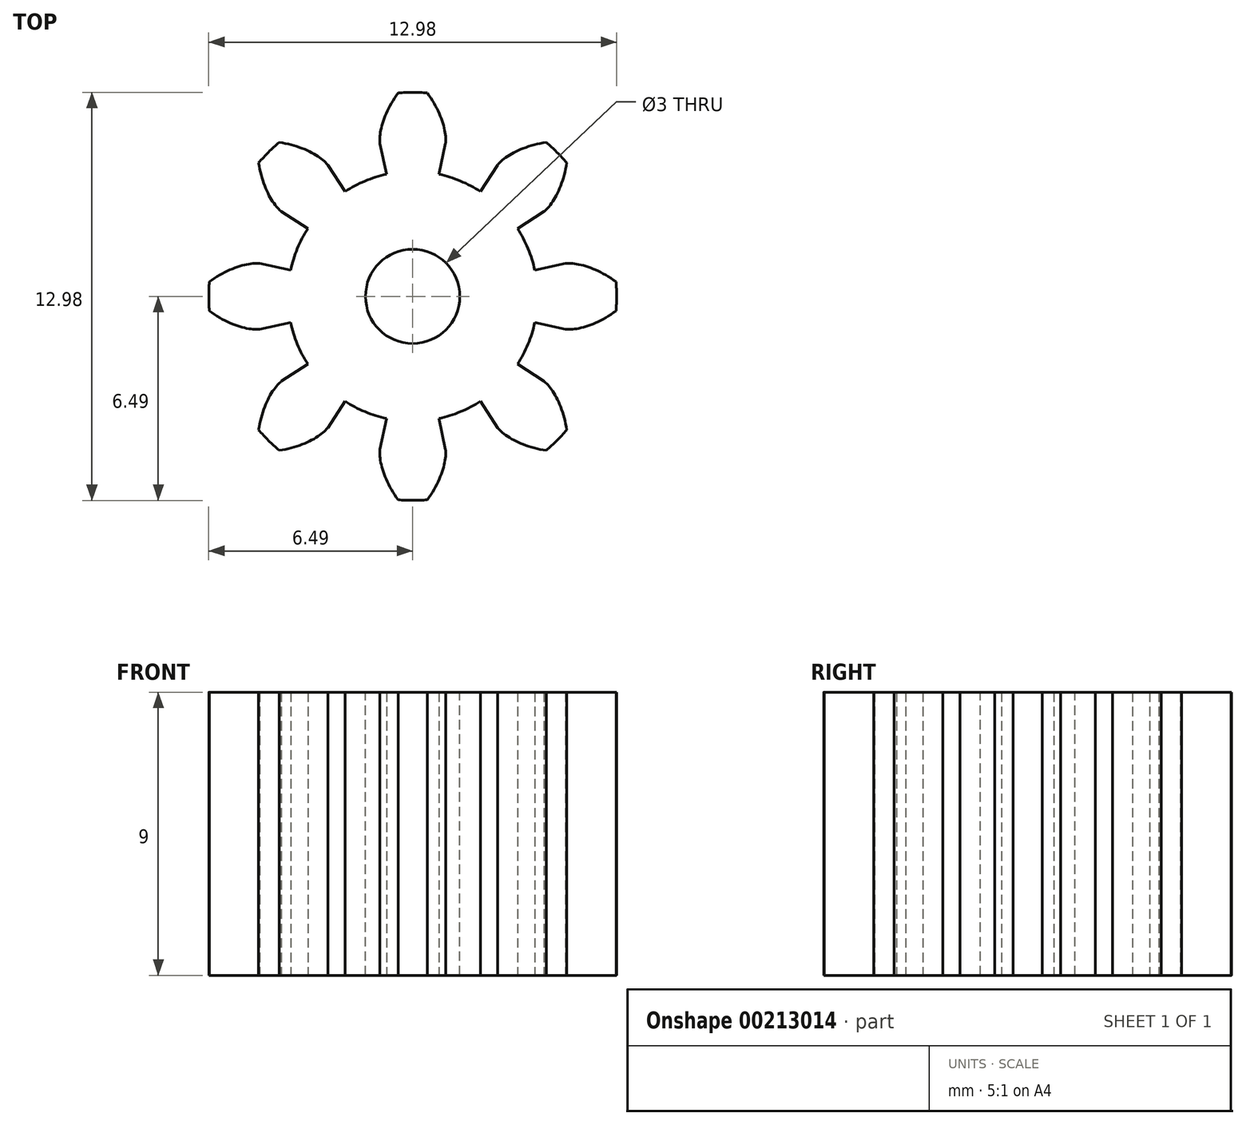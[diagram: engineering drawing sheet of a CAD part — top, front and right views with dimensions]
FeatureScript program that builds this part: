
annotation { "Feature Type Name" : "Feature", "Feature Type Description" : "" }
export const myFeature = defineFeature(function(context is Context, id is Id, definition is map)
    precondition{}
    {
        {
            var Q0;
            Q0=qCreatedBy(makeId("Top.planeOp"),FACE);
            var sketch = newSketch(context, id + "F0", { "sketchPlane" : qUnion([Q0])});
            skCircle(sketch, "E0", {"center": v(0, 0) * mm, "radius": 4.97 * mm, "construction": true});
            skLineSegment(sketch, "E1", {"start": v(4.97, 0) * mm, "end": v(4.97, 0) * mm});
            skLineSegment(sketch, "E2", {"start": v(0, 0) * mm, "end": v(4.96, 0.42) * mm, "construction": true});
            skLineSegment(sketch, "E3", {"start": v(4.96, 0.42) * mm, "end": v(5, 0) * mm, "construction": true});
            skLineSegment(sketch, "E4", {"start": v(0, 0) * mm, "end": v(4.9, 0.85) * mm, "construction": true});
            skLineSegment(sketch, "E5", {"start": v(4.9, 0.85) * mm, "end": v(5.05, 0) * mm, "construction": true});
            skLineSegment(sketch, "E6", {"start": v(0, 0) * mm, "end": v(4.81, 1.26) * mm, "construction": true});
            skLineSegment(sketch, "E7", {"start": v(4.81, 1.26) * mm, "end": v(5.14, 0.03) * mm, "construction": true});
            skLineSegment(sketch, "E8", {"start": v(0, 0) * mm, "end": v(4.69, 1.67) * mm, "construction": true});
            skLineSegment(sketch, "E9", {"start": v(4.69, 1.67) * mm, "end": v(5.26, 0.07) * mm, "construction": true});
            skLineSegment(sketch, "E10", {"start": v(0, 0) * mm, "end": v(4.53, 2.06) * mm, "construction": true});
            skLineSegment(sketch, "E11", {"start": v(4.53, 2.06) * mm, "end": v(5.4, 0.13) * mm, "construction": true});
            skLineSegment(sketch, "E12", {"start": v(0, 0) * mm, "end": v(4.33, 2.44) * mm, "construction": true});
            skLineSegment(sketch, "E13", {"start": v(4.33, 2.44) * mm, "end": v(5.59, 0.22) * mm, "construction": true});
            skLineSegment(sketch, "E14", {"start": v(0, 0) * mm, "end": v(4.1, 2.8) * mm, "construction": true});
            skLineSegment(sketch, "E15", {"start": v(4.1, 2.8) * mm, "end": v(5.79, 0.34) * mm, "construction": true});
            skLineSegment(sketch, "E16", {"start": v(0, 0) * mm, "end": v(3.86, 3.14) * mm, "construction": true});
            skLineSegment(sketch, "E17", {"start": v(3.86, 3.14) * mm, "end": v(6, 0.5) * mm, "construction": true});
            skLineSegment(sketch, "E18", {"start": v(0, 0) * mm, "end": v(3.57, 3.46) * mm, "construction": true});
            skLineSegment(sketch, "E19", {"start": v(3.57, 3.46) * mm, "end": v(6.24, 0.71) * mm, "construction": true});
            skLineSegment(sketch, "E20", {"start": v(0, 0) * mm, "end": v(3.26, 3.75) * mm, "construction": true});
            skLineSegment(sketch, "E21", {"start": v(3.26, 3.75) * mm, "end": v(6.47, 0.96) * mm, "construction": true});
            skPoint(sketch, "E22", {"position": v(4.97, 0) * mm});
            skCircle(sketch, "E23", {"center": v(0, 0) * mm, "radius": 3.97 * mm});
            skLineSegment(sketch, "E24", {"start": v(3.97, 0) * mm, "end": v(4.97, 0) * mm});
            skFitSpline(sketch, "E25", {"points": [v(4.97, 0) * mm, v(5, 0) * mm, v(5.05, 0) * mm, v(5.14, 0.03) * mm, v(5.26, 0.07) * mm, v(5.4, 0.13) * mm, v(5.59, 0.22) * mm, v(5.79, 0.34) * mm, v(6, 0.5) * mm, v(6.24, 0.71) * mm, v(6.47, 0.96) * mm], "startDerivative": vector(0.48, 0.02) * mm, "endDerivative": vector(1.62, 1.77) * mm});
            skFitSpline(sketch, "E26", {"points": [v(4.97, 0) * mm, v(5, 0) * mm, v(5.05, 0) * mm, v(5.14, 0.03) * mm, v(5.26, 0.07) * mm, v(5.4, 0.13) * mm, v(5.59, 0.22) * mm, v(5.79, 0.34) * mm, v(6, 0.5) * mm, v(6.24, 0.71) * mm, v(6.47, 0.96) * mm], "startDerivative": vector(0.48, 0.02) * mm, "endDerivative": vector(1.62, 1.77) * mm, "construction": true});
            skLineSegment(sketch, "E27", {"start": v(0, 0) * mm, "end": v(9.9, 2.12) * mm, "construction": true});
            skLineSegment(sketch, "E28.MirrorCS", {"start": v(3.62, 1.63) * mm, "end": v(4.54, 2.04) * mm});
            skFitSpline(sketch, "E29.MirrorCS", {"points": [v(4.54, 2.04) * mm, v(4.55, 2.05) * mm, v(4.6, 2.06) * mm, v(4.7, 2.08) * mm, v(4.82, 2.1) * mm, v(4.99, 2.1) * mm, v(5.19, 2.1) * mm, v(5.42, 2.06) * mm, v(5.69, 2) * mm, v(5.98, 1.9) * mm, v(6.3, 1.78) * mm], "startDerivative": vector(0.44, 0.18) * mm, "endDerivative": vector(2.2, -0.95) * mm});
            skArc(sketch, "E30", {"start": v(6.23, 1.8) * mm, "mid": v(-6.34, -1.36) * mm, "end": v(6.42, 0.9) * mm, "construction": true});
            skArc(sketch, "E31", {"start": v(6.42, 0.9) * mm, "mid": v(6.34, 1.36) * mm, "end": v(6.23, 1.8) * mm});
            skSolve(sketch);
        }
        {
            var Q0;
            Q0=qCreatedBy(makeId("Front.planeOp"),FACE);
            var sketch = newSketch(context, id + "F1", { "sketchPlane" : qUnion([Q0])});
            skLineSegment(sketch, "E32", {"start": v(0, 0) * mm, "end": v(0, 25.92) * mm});
            skSolve(sketch);
        }
        {
            var Q0;
            {var subQ0=sQuery(id+"F0.wireOp",EDGE,"E23");var subQ1=makeQuery(id+"F0.imprint","INTERSECT",VERTEX,{"derivedFrom":[subQ0,sQuery(id+"F0.wireOp",EDGE,"E24")]});Q0=makeQuery(id+"F0.imprint","IMPRINT",FACE,{"disambiguationData":[TD([[makeQuery(id+"F0.imprint","IMPRINT",EDGE,{"disambiguationData":[TD([[subQ1,-1.0]])],"derivedFrom":subQ0}),1.0]])]});}
            var Q1;
            {var subQ1=sQuery(id+"F0.wireOp",EDGE,"E24");Q1=makeQuery(id+"F0.imprint","IMPRINT",FACE,{"disambiguationData":[TD([[makeQuery(id+"F0.imprint","IMPRINT",EDGE,{"derivedFrom":subQ1}),1.0]])]});}
            extrude(context, id + "F2", {"entities" : qUnion([Q0, Q1]), "depth" : 9 * mm});
        }
        {
            var Q0;
            Q0=makeQuery(id+"F2.opExtrude","SWEPT_BODY",BODY,{"disambiguationData":[OSD([sQuery(id+"F0.wireOp",EDGE,"E23"),sQuery(id+"F0.wireOp",EDGE,"E24"),sQuery(id+"F0.wireOp",EDGE,"E25"),sQuery(id+"F0.wireOp",EDGE,"E28.MirrorCS"),sQuery(id+"F0.wireOp",EDGE,"E29.MirrorCS"),sQuery(id+"F0.wireOp",EDGE,"E31")])]});
            var Q1;
            Q1=sQuery(id+"F1.wireOp",EDGE,"E32");
            circularPattern(context, id + "F3", {"operationType" : NewBodyOperationType.ADD, "entities" : qUnion([Q0]), "axis" : qUnion([Q1]), "angle" : 360 * degree, "instanceCount" : 8, "equalSpace" : true});
        }
        {
            var Q0;
            Q0=makeQuery(id+"F2.opExtrude","SWEPT_BODY",BODY,{"disambiguationData":[OSD([sQuery(id+"F0.wireOp",EDGE,"E23"),sQuery(id+"F0.wireOp",EDGE,"E24"),sQuery(id+"F0.wireOp",EDGE,"E25"),sQuery(id+"F0.wireOp",EDGE,"E28.MirrorCS"),sQuery(id+"F0.wireOp",EDGE,"E29.MirrorCS"),sQuery(id+"F0.wireOp",EDGE,"E31")])]});
            var Q1;
            Q1=sQuery(id+"F1.wireOp",EDGE,"E32");
            transform(context, id + "F4", {"entities" : qUnion([Q0]), "transformType" : TransformType.ROTATION, "transformAxis" : qUnion([Q1]), "angle" : 12.1 * degree, "oppositeDirection" : true, "makeCopy" : false});
        }
        {
            var Q0;
            {var subQ0=makeQuery(id+"F2.opExtrude","CAP_FACE",FACE,{"disambiguationData":[OSD([sQuery(id+"F0.wireOp",EDGE,"E23"),sQuery(id+"F0.wireOp",EDGE,"E24"),sQuery(id+"F0.wireOp",EDGE,"E25"),sQuery(id+"F0.wireOp",EDGE,"E28.MirrorCS"),sQuery(id+"F0.wireOp",EDGE,"E29.MirrorCS"),sQuery(id+"F0.wireOp",EDGE,"E31")])],"isStart":false});Q0=makeQuery(id+"F3.boolean.opBoolean","MERGE",FACE,{"derivedFrom":[subQ0,makeQuery(id+"F3.opPattern","COPY",FACE,{"derivedFrom":subQ0,"instanceName":"1"}),makeQuery(id+"F3.opPattern","COPY",FACE,{"derivedFrom":subQ0,"instanceName":"2"}),makeQuery(id+"F3.opPattern","COPY",FACE,{"derivedFrom":subQ0,"instanceName":"3"}),makeQuery(id+"F3.opPattern","COPY",FACE,{"derivedFrom":subQ0,"instanceName":"4"}),makeQuery(id+"F3.opPattern","COPY",FACE,{"derivedFrom":subQ0,"instanceName":"5"}),makeQuery(id+"F3.opPattern","COPY",FACE,{"derivedFrom":subQ0,"instanceName":"6"}),makeQuery(id+"F3.opPattern","COPY",FACE,{"derivedFrom":subQ0,"instanceName":"7"})]});}
            var sketch = newSketch(context, id + "F5", { "sketchPlane" : qUnion([Q0])});
            skCircle(sketch, "E33", {"center": v(0, 0) * mm, "radius": 1.5 * mm});
            skSolve(sketch);
        }
        {
            var Q0;
            Q0=makeQuery(id+"F5.imprint","IMPRINT",FACE,{"disambiguationData":[TD([[makeQuery(id+"F5.imprint","IMPRINT",EDGE,{"derivedFrom":sQuery(id+"F5.wireOp",EDGE,"E33")}),1.0]])]});
            extrude(context, id + "F6", {"entities" : qUnion([Q0]), "operationType" : NewBodyOperationType.REMOVE, "endBound" : BoundingType.UP_TO_NEXT, "oppositeDirection" : true, "depth" : 25 * mm});
        }
    });
